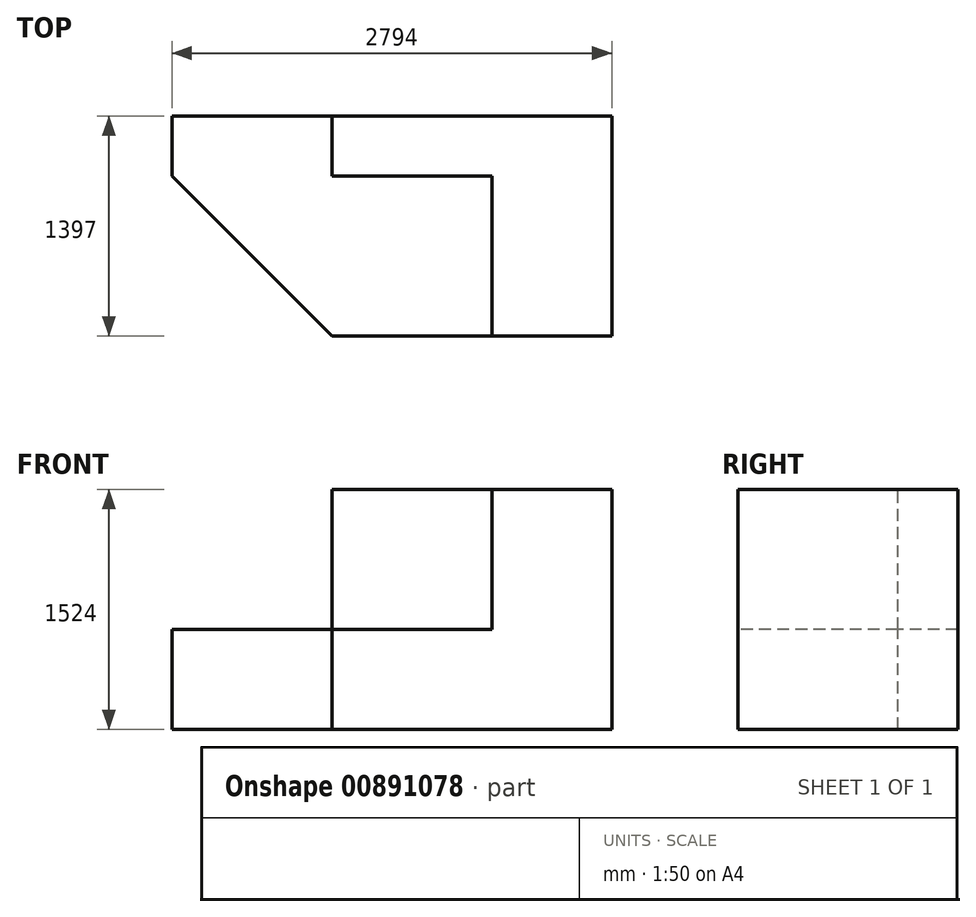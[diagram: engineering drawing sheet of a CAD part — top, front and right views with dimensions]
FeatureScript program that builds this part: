
annotation { "Feature Type Name" : "Feature", "Feature Type Description" : "" }
export const myFeature = defineFeature(function(context is Context, id is Id, definition is map)
    precondition{}
    {
        {
            var Q0;
            Q0=qCreatedBy(makeId("Front.planeOp"),FACE);
            var sketch = newSketch(context, id + "F0", { "sketchPlane" : qUnion([Q0])});
            skLineSegment(sketch, "E0.bottom", {"start": v(0, 0) * mm, "end": v(-2794, 0) * mm});
            skLineSegment(sketch, "E0.top", {"start": v(0, 1524) * mm, "end": v(-2794, 1524) * mm});
            skLineSegment(sketch, "E0.left", {"start": v(0, 0) * mm, "end": v(0, 1524) * mm});
            skLineSegment(sketch, "E0.right", {"start": v(-2794, 0) * mm, "end": v(-2794, 1524) * mm});
            skSolve(sketch);
        }
        {
            var Q0;
            Q0 = qSketchRegion(id + "F0", true);
            var Q1;
            Q1=makeQuery(id+"F0.imprint","IMPRINT",FACE,{"disambiguationData":[TD([[makeQuery(id+"F0.imprint","IMPRINT",EDGE,{"derivedFrom":sQuery(id+"F0.wireOp",EDGE,"E0.bottom")}),-1.0]])]});
            extrude(context, id + "F1", {"entities" : qUnion([Q0, Q1]), "oppositeDirection" : true, "depth" : 1397 * mm, "offsetDistance" : 25.4 * mm});
        }
        {
            var Q0;
            Q0=makeQuery(id+"F1.opExtrude","SWEPT_FACE",FACE,{"disambiguationData":[OSD([sQuery(id+"F0.wireOp",EDGE,"E0.top")])]});
            var sketch = newSketch(context, id + "F2", { "sketchPlane" : qUnion([Q0])});
            skLineSegment(sketch, "E1", {"start": v(0, 1397) * mm, "end": v(-1778, 1397) * mm});
            skLineSegment(sketch, "E2", {"start": v(-1778, 1397) * mm, "end": v(-1778, 1016) * mm});
            skLineSegment(sketch, "E3", {"start": v(-1778, 1016) * mm, "end": v(-762, 1016) * mm});
            skLineSegment(sketch, "E4", {"start": v(-762, 1016) * mm, "end": v(-762, 0) * mm});
            skSolve(sketch);
        }
        {
            var Q0;
            Q0 = qSketchRegion(id + "F2", true);
            var Q1;
            {var subQ3=sQuery(id+"F2.wireOp",EDGE,"E2");Q1=makeQuery(id+"F2.imprint","IMPRINT",FACE,{"disambiguationData":[TD([[makeQuery(id+"F2.imprint","IMPRINT",EDGE,{"derivedFrom":subQ3}),-1.0]])]});}
            extrude(context, id + "F3", {"entities" : qUnion([Q0, Q1]), "operationType" : NewBodyOperationType.REMOVE, "oppositeDirection" : true, "depth" : 889 * mm, "offsetDistance" : 25.4 * mm});
        }
        {
            var Q0;
            Q0=makeQuery(id+"F3.boolean.opBoolean","COPY",FACE,{"derivedFrom":makeQuery(id+"F3.opExtrude","CAP_FACE",FACE,{"disambiguationData":[OSD([sQuery(id+"F0.wireOp",EDGE,"E0.top"),sQuery(id+"F0.wireOp",EDGE,"E0.right"),sQuery(id+"F2.wireOp",EDGE,"E2"),sQuery(id+"F2.wireOp",EDGE,"E3"),sQuery(id+"F2.wireOp",EDGE,"E4")])],"isStart":false})});
            var sketch = newSketch(context, id + "F4", { "sketchPlane" : qUnion([Q0])});
            skLineSegment(sketch, "E5", {"start": v(-2794, 1016) * mm, "end": v(-1778, 0) * mm});
            skSolve(sketch);
        }
        {
            var Q0;
            Q0 = qSketchRegion(id + "F4", true);
            var Q1;
            {var subQ0=sQuery(id+"F4.wireOp",EDGE,"E5");Q1=makeQuery(id+"F4.imprint","IMPRINT",FACE,{"disambiguationData":[TD([[makeQuery(id+"F4.imprint","IMPRINT",EDGE,{"derivedFrom":subQ0}),-1.0]])]});}
            extrude(context, id + "F5", {"entities" : qUnion([Q0, Q1]), "operationType" : NewBodyOperationType.REMOVE, "oppositeDirection" : true, "depth" : 1270 * mm, "offsetDistance" : 25.4 * mm});
        }
    });
